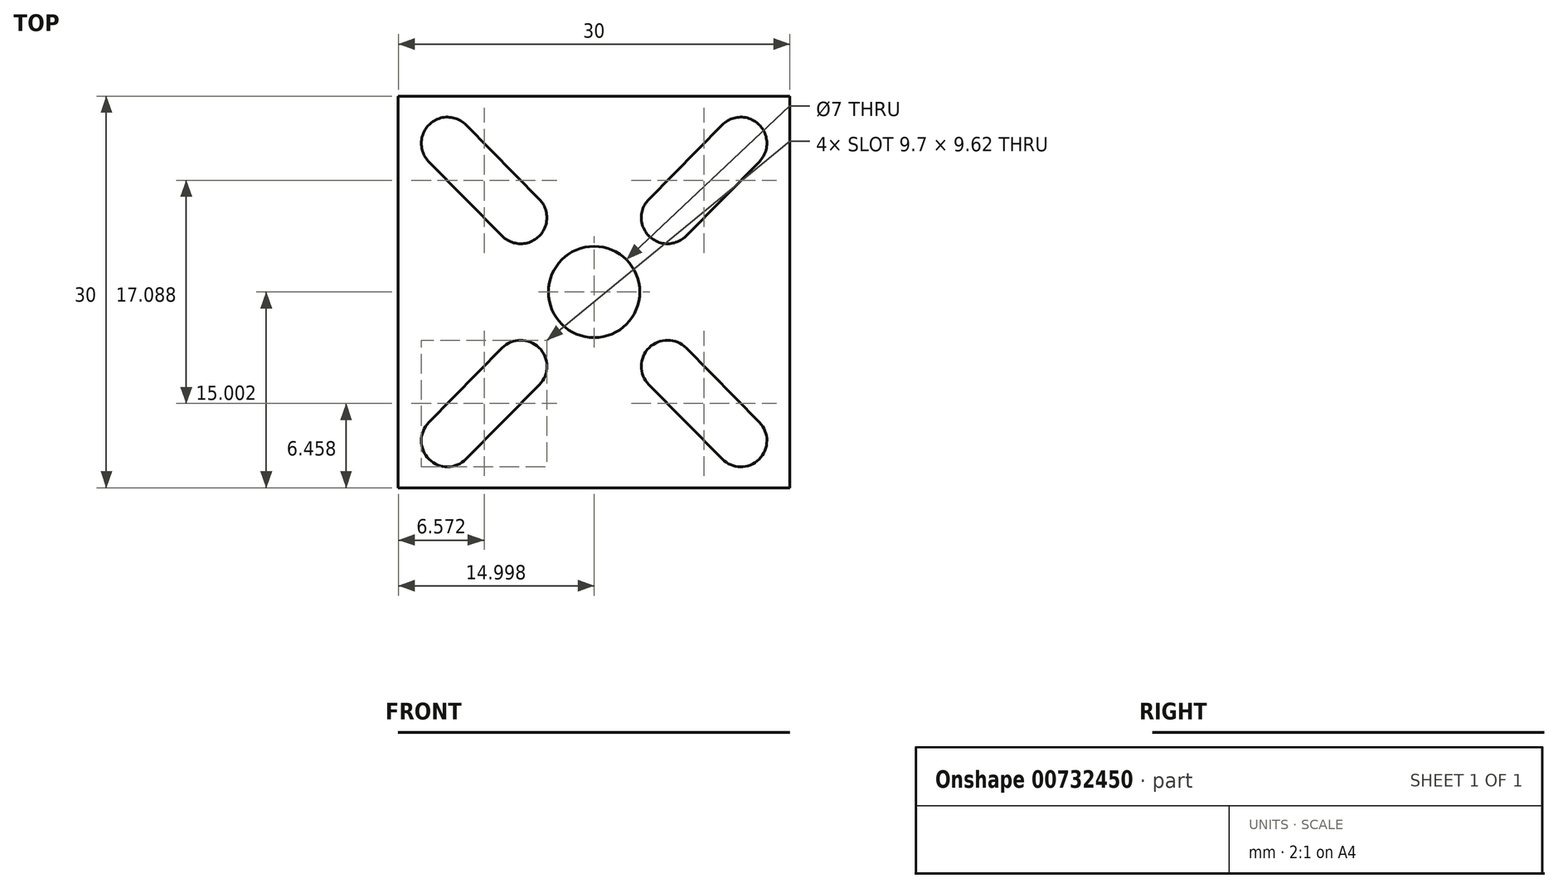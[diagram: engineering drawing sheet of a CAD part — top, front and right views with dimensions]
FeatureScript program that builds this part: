
annotation { "Feature Type Name" : "Feature", "Feature Type Description" : "" }
export const myFeature = defineFeature(function(context is Context, id is Id, definition is map)
    precondition{}
    {
        {
            var Q0;
            Q0=qCreatedBy(makeId("Top.planeOp"), FACE);
            var sketch = newSketch(context, id + "F0", { "sketchPlane" : qUnion([Q0])});
            skLineSegment(sketch, "E0.bottom", {"start": v(-16.16, -15.85) * mm, "end": v(13.84, -15.85) * mm});
            skLineSegment(sketch, "E0.top", {"start": v(-16.16, 14.15) * mm, "end": v(13.84, 14.15) * mm});
            skLineSegment(sketch, "E0.left", {"start": v(-16.16, -15.85) * mm, "end": v(-16.16, 14.15) * mm});
            skLineSegment(sketch, "E0.right", {"start": v(13.84, -15.85) * mm, "end": v(13.84, 14.15) * mm});
            skPoint(sketch, "E0.middle", {"position": v(-1.16, -0.85) * mm});
            skCircle(sketch, "E1", {"center": v(-1.16, -0.85) * mm, "radius": 3 * mm});
            skCircle(sketch, "E2", {"center": v(-1.16, -0.85) * mm, "radius": 3.5 * mm});
            skArc(sketch, "E3", {"start": v(-8.2, 3.44) * mm, "mid": v(-5.38, 3.42) * mm, "end": v(-5.36, 6.25) * mm});
            skArc(sketch, "E4", {"start": v(-10.97, 11.95) * mm, "mid": v(-13.8, 11.97) * mm, "end": v(-13.82, 9.14) * mm});
            skLineSegment(sketch, "E5", {"start": v(-13.82, 9.14) * mm, "end": v(-8.2, 3.44) * mm});
            skLineSegment(sketch, "E6", {"start": v(-5.36, 6.25) * mm, "end": v(-10.97, 11.95) * mm});
            skArc(sketch, "E7.MirrorCS", {"start": v(8.65, 11.95) * mm, "mid": v(11.48, 11.97) * mm, "end": v(11.5, 9.14) * mm});
            skLineSegment(sketch, "E8.MirrorCS", {"start": v(11.5, 9.14) * mm, "end": v(5.88, 3.44) * mm});
            skLineSegment(sketch, "E9.MirrorCS", {"start": v(3.03, 6.25) * mm, "end": v(8.65, 11.95) * mm});
            skArc(sketch, "E10.MirrorCS", {"start": v(5.88, 3.44) * mm, "mid": v(3.05, 3.42) * mm, "end": v(3.03, 6.25) * mm});
            skArc(sketch, "E11.MirrorCS", {"start": v(-8.2, -5.14) * mm, "mid": v(-5.38, -5.12) * mm, "end": v(-5.36, -7.95) * mm});
            skLineSegment(sketch, "E12.MirrorCS", {"start": v(-13.82, -10.84) * mm, "end": v(-8.2, -5.14) * mm});
            skArc(sketch, "E13.MirrorCS", {"start": v(-10.97, -13.64) * mm, "mid": v(-13.8, -13.66) * mm, "end": v(-13.82, -10.84) * mm});
            skLineSegment(sketch, "E14.MirrorCS", {"start": v(-5.36, -7.95) * mm, "end": v(-10.97, -13.64) * mm});
            skArc(sketch, "E15.MirrorCS", {"start": v(5.88, -5.14) * mm, "mid": v(3.05, -5.12) * mm, "end": v(3.03, -7.95) * mm});
            skLineSegment(sketch, "E16.MirrorCS", {"start": v(11.5, -10.84) * mm, "end": v(5.88, -5.14) * mm});
            skLineSegment(sketch, "E17.MirrorCS", {"start": v(3.03, -7.95) * mm, "end": v(8.65, -13.64) * mm});
            skArc(sketch, "E18.MirrorCS", {"start": v(8.65, -13.64) * mm, "mid": v(11.48, -13.66) * mm, "end": v(11.5, -10.84) * mm});
            skSolve(sketch);
        }
        {
            var Q0;
            Q0 = qSketchRegion(id + "F0", true);
            extrude(context, id + "F1", {"entities" : qUnion([Q0]), "depth" : 1 / 406.4 * mm, "offsetDistance" : 25 * mm});
        }
    });
